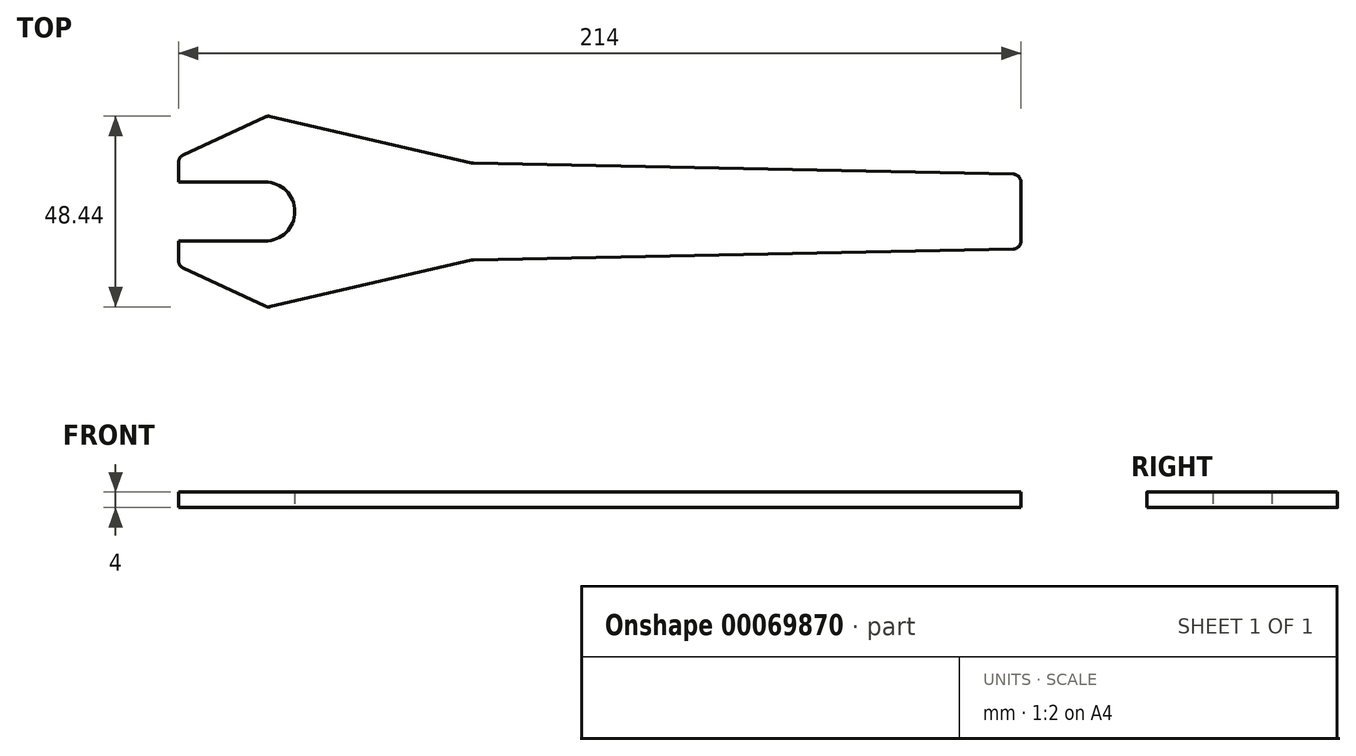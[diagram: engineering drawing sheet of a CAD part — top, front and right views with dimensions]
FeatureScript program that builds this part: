
annotation { "Feature Type Name" : "Feature", "Feature Type Description" : "" }
export const myFeature = defineFeature(function(context is Context, id is Id, definition is map)
    precondition{}
    {
        {
            var Q0;
            Q0=qCreatedBy(makeId("Top.planeOp"),FACE);
            var sketch = newSketch(context, id + "F0", { "sketchPlane" : qUnion([Q0])});
            skLineSegment(sketch, "E0", {"start": v(-55.2, 3.38) * mm, "end": v(-33.2, 3.38) * mm});
            skLineSegment(sketch, "E1", {"start": v(-33.2, 3.38) * mm, "end": v(-33.2, -11.62) * mm, "construction": true});
            skLineSegment(sketch, "E2", {"start": v(-33.2, -11.62) * mm, "end": v(-55.2, -11.62) * mm});
            skArc(sketch, "E3", {"start": v(-33.2, -11.62) * mm, "mid": v(-25.7, -4.12) * mm, "end": v(-33.2, 3.38) * mm});
            skLineSegment(sketch, "E4", {"start": v(-55.2, 3.38) * mm, "end": v(-55.2, 8.38) * mm});
            skLineSegment(sketch, "E5", {"start": v(-54.05, 10.2) * mm, "end": v(-33.2, 19.92) * mm});
            skLineSegment(sketch, "E6", {"start": v(-31.9, 20.05) * mm, "end": v(19.28, 8.24) * mm});
            skLineSegment(sketch, "E7", {"start": v(19.69, 8.18) * mm, "end": v(156.84, 5.38) * mm});
            skLineSegment(sketch, "E8", {"start": v(158.8, 3.38) * mm, "end": v(158.8, -11.62) * mm});
            skLineSegment(sketch, "E9", {"start": v(156.84, -13.62) * mm, "end": v(19.69, -16.42) * mm});
            skLineSegment(sketch, "E10", {"start": v(19.28, -16.47) * mm, "end": v(-31.9, -28.29) * mm});
            skLineSegment(sketch, "E11", {"start": v(-33.2, -28.15) * mm, "end": v(-54.05, -18.43) * mm});
            skLineSegment(sketch, "E12", {"start": v(-55.2, -16.62) * mm, "end": v(-55.2, -11.62) * mm});
            skPoint(sketch, "E13.visualSharp", {"position": v(-55.2, 9.66) * mm});
            skArc(sketch, "E13.filletArc", {"start": v(-54.05, 10.2) * mm, "mid": v(-54.89, 9.46) * mm, "end": v(-55.2, 8.38) * mm});
            skPoint(sketch, "E14.visualSharp", {"position": v(-32.58, 20.2) * mm});
            skArc(sketch, "E14.filletArc", {"start": v(-31.9, 20.05) * mm, "mid": v(-32.56, 20.1) * mm, "end": v(-33.2, 19.92) * mm});
            skPoint(sketch, "E15.visualSharp", {"position": v(19.48, 8.19) * mm});
            skArc(sketch, "E15.filletArc", {"start": v(19.28, 8.24) * mm, "mid": v(19.48, 8.2) * mm, "end": v(19.69, 8.18) * mm});
            skPoint(sketch, "E16.visualSharp", {"position": v(158.8, 5.34) * mm});
            skArc(sketch, "E16.filletArc", {"start": v(158.8, 3.38) * mm, "mid": v(158.23, 4.78) * mm, "end": v(156.84, 5.38) * mm});
            skPoint(sketch, "E17.visualSharp", {"position": v(158.8, -13.58) * mm});
            skArc(sketch, "E17.filletArc", {"start": v(156.84, -13.62) * mm, "mid": v(158.23, -13.02) * mm, "end": v(158.8, -11.62) * mm});
            skPoint(sketch, "E18.visualSharp", {"position": v(19.48, -16.42) * mm});
            skArc(sketch, "E18.filletArc", {"start": v(19.69, -16.42) * mm, "mid": v(19.48, -16.43) * mm, "end": v(19.28, -16.47) * mm});
            skPoint(sketch, "E19.visualSharp", {"position": v(-32.58, -28.44) * mm});
            skArc(sketch, "E19.filletArc", {"start": v(-33.2, -28.15) * mm, "mid": v(-32.56, -28.33) * mm, "end": v(-31.9, -28.29) * mm});
            skPoint(sketch, "E20.visualSharp", {"position": v(-55.2, -17.9) * mm});
            skArc(sketch, "E20.filletArc", {"start": v(-55.2, -16.62) * mm, "mid": v(-54.89, -17.7) * mm, "end": v(-54.05, -18.43) * mm});
            skLineSegment(sketch, "E21", {"start": v(156.8, 3.38) * mm, "end": v(156.8, -11.62) * mm, "construction": true});
            skLineSegment(sketch, "E22", {"start": v(156.8, -4.12) * mm, "end": v(-33.2, -4.12) * mm, "construction": true});
            skLineSegment(sketch, "E23", {"start": v(19.69, 8.18) * mm, "end": v(19.69, -16.42) * mm, "construction": true});
            skPoint(sketch, "E24", {"position": v(19.69, -4.12) * mm});
            skLineSegment(sketch, "E25", {"start": v(-33.2, 19.92) * mm, "end": v(-33.2, -28.15) * mm, "construction": true});
            skCircle(sketch, "E26", {"center": v(-33.2, -4.12) * mm, "radius": 21.78 * mm, "construction": true});
            skSolve(sketch);
        }
        {
            var Q0;
            Q0 = qSketchRegion(id + "F0", true);
            extrude(context, id + "F1", {"entities" : qUnion([Q0]), "depth" : 4 * mm});
        }
    });
